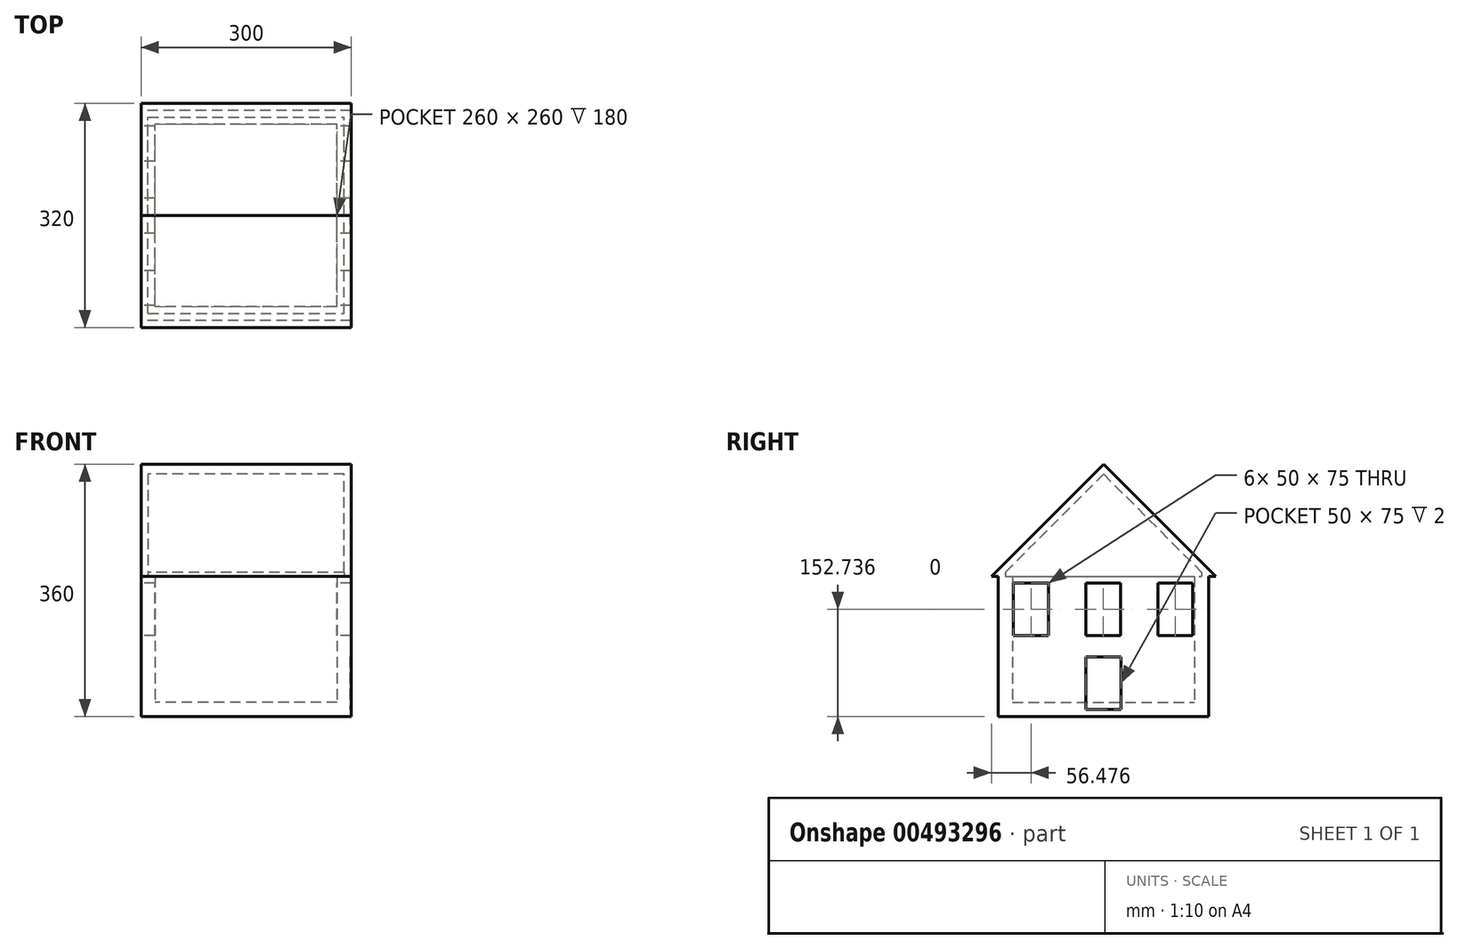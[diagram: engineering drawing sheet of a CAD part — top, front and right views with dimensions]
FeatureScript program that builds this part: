
annotation { "Feature Type Name" : "Feature", "Feature Type Description" : "" }
export const myFeature = defineFeature(function(context is Context, id is Id, definition is map)
    precondition{}
    {
        {
            var Q0;
            Q0=qCreatedBy(makeId("Top.planeOp"),FACE);
            var sketch = newSketch(context, id + "F0", { "sketchPlane" : qUnion([Q0])});
            skLineSegment(sketch, "E0.bottom", {"start": v(150, -150) * mm, "end": v(-150, -150) * mm});
            skLineSegment(sketch, "E0.top", {"start": v(150, 150) * mm, "end": v(-150, 150) * mm});
            skLineSegment(sketch, "E0.left", {"start": v(150, -150) * mm, "end": v(150, 150) * mm});
            skLineSegment(sketch, "E0.right", {"start": v(-150, -150) * mm, "end": v(-150, 150) * mm});
            skPoint(sketch, "E0.middle", {"position": v(0, 0) * mm});
            skSolve(sketch);
        }
        {
            var Q0;
            Q0=makeQuery(id+"F0.imprint","IMPRINT",FACE,{"disambiguationData":[TD([[makeQuery(id+"F0.imprint","IMPRINT",EDGE,{"derivedFrom":sQuery(id+"F0.wireOp",EDGE,"E0.bottom")}),-1.0]])]});
            extrude(context, id + "F1", {"entities" : qUnion([Q0]), "depth" : 200 * mm});
        }
        {
            var Q0;
            Q0=makeQuery(id+"F1.opExtrude","CAP_FACE",FACE,{"disambiguationData":[OSD([sQuery(id+"F0.wireOp",EDGE,"E0.bottom"),sQuery(id+"F0.wireOp",EDGE,"E0.top"),sQuery(id+"F0.wireOp",EDGE,"E0.left"),sQuery(id+"F0.wireOp",EDGE,"E0.right")])],"isStart":false});
            shell(context, id + "F2", {"entities" : qUnion([Q0]), "thickness" : 20 * mm});
        }
        {
            var Q0;
            Q0=qCreatedBy(makeId("Right.planeOp"),FACE);
            var sketch = newSketch(context, id + "F3", { "sketchPlane" : qUnion([Q0])});
            skLineSegment(sketch, "E1", {"start": v(0, 360) * mm, "end": v(160, 200) * mm});
            skLineSegment(sketch, "E2", {"start": v(160, 200) * mm, "end": v(-160, 200) * mm});
            skLineSegment(sketch, "E3", {"start": v(-160, 200) * mm, "end": v(0, 360) * mm});
            skSolve(sketch);
        }
        {
            var Q0;
            Q0 = qSketchRegion(id + "F3", true);
            extrude(context, id + "F4", {"entities" : qUnion([Q0]), "operationType" : NewBodyOperationType.ADD, "depth" : 300 * mm, "symmetric" : true});
        }
        {
            var Q0;
            Q0=makeQuery(id+"F4.boolean.opBoolean","MERGE",FACE,{"derivedFrom":[makeQuery(id+"F1.opExtrude","SWEPT_FACE",FACE,{"disambiguationData":[OSD([sQuery(id+"F0.wireOp",EDGE,"E0.right")])]}),makeQuery(id+"F4.opExtrude","CAP_FACE",FACE,{"disambiguationData":[OSD([sQuery(id+"F3.wireOp",EDGE,"E1"),sQuery(id+"F3.wireOp",EDGE,"E2"),sQuery(id+"F3.wireOp",EDGE,"E3")])],"isStart":true})]});
            var sketch = newSketch(context, id + "F5", { "sketchPlane" : qUnion([Q0])});
            skLineSegment(sketch, "E4.bottom", {"start": v(-77.48, 115.24) * mm, "end": v(-127.48, 115.24) * mm});
            skLineSegment(sketch, "E4.top", {"start": v(-77.48, 190.24) * mm, "end": v(-127.48, 190.24) * mm});
            skLineSegment(sketch, "E4.left", {"start": v(-77.48, 115.24) * mm, "end": v(-77.48, 190.24) * mm});
            skLineSegment(sketch, "E4.right", {"start": v(-127.48, 115.24) * mm, "end": v(-127.48, 190.24) * mm});
            skPoint(sketch, "E4.middle", {"position": v(-102.48, 152.74) * mm});
            skLineSegment(sketch, "E5.1.0.0", {"start": v(-24.48, 115.24) * mm, "end": v(-24.48, 190.24) * mm});
            skLineSegment(sketch, "E5.1.0.1", {"start": v(25.52, 115.24) * mm, "end": v(25.52, 190.24) * mm});
            skLineSegment(sketch, "E5.1.0.2", {"start": v(25.52, 190.24) * mm, "end": v(-24.48, 190.24) * mm});
            skLineSegment(sketch, "E5.1.0.3", {"start": v(25.52, 115.24) * mm, "end": v(-24.48, 115.24) * mm});
            skPoint(sketch, "E5.1.0.4", {"position": v(0.52, 152.74) * mm});
            skLineSegment(sketch, "E5.2.0.0", {"start": v(78.52, 115.24) * mm, "end": v(78.52, 190.24) * mm});
            skLineSegment(sketch, "E5.2.0.1", {"start": v(128.52, 115.24) * mm, "end": v(128.52, 190.24) * mm});
            skLineSegment(sketch, "E5.2.0.2", {"start": v(128.52, 190.24) * mm, "end": v(78.52, 190.24) * mm});
            skLineSegment(sketch, "E5.2.0.3", {"start": v(128.52, 115.24) * mm, "end": v(78.52, 115.24) * mm});
            skPoint(sketch, "E5.2.0.4", {"position": v(103.52, 152.74) * mm});
            skLineSegment(sketch, "E5.direction1", {"start": v(-127.48, 115.24) * mm, "end": v(-24.48, 115.24) * mm, "construction": true});
            skSolve(sketch);
        }
        {
            var Q0;
            Q0 = qSketchRegion(id + "F5", true);
            extrude(context, id + "F6", {"entities" : qUnion([Q0]), "operationType" : NewBodyOperationType.REMOVE, "endBound" : BoundingType.THROUGH_ALL, "oppositeDirection" : true, "depth" : 25 * mm});
        }
        {
            var Q0;
            Q0=makeQuery(id+"F4.boolean.opBoolean","SPLIT",FACE,{"disambiguationData":[TD([makeQuery(id+"F2.opShell","OFFSET_FACE",FACE,{"disambiguationData":[OSD([sQuery(id+"F0.wireOp",EDGE,"E0.bottom")])]})])],"derivedFrom":makeQuery(id+"F4.opExtrude","SWEPT_FACE",FACE,{"disambiguationData":[OSD([sQuery(id+"F3.wireOp",EDGE,"E2")])]})});
            shell(context, id + "F7", {"entities" : qUnion([Q0]), "thickness" : 10 * mm});
        }
        {
            var Q0;
            Q0=makeQuery(id+"F4.boolean.opBoolean","MERGE",FACE,{"derivedFrom":[makeQuery(id+"F1.opExtrude","SWEPT_FACE",FACE,{"disambiguationData":[OSD([sQuery(id+"F0.wireOp",EDGE,"E0.left")])]}),makeQuery(id+"F4.opExtrude","CAP_FACE",FACE,{"disambiguationData":[OSD([sQuery(id+"F3.wireOp",EDGE,"E1"),sQuery(id+"F3.wireOp",EDGE,"E2"),sQuery(id+"F3.wireOp",EDGE,"E3")])],"isStart":false})]});
            var sketch = newSketch(context, id + "F8", { "sketchPlane" : qUnion([Q0])});
            skLineSegment(sketch, "E6.bottom", {"start": v(25, 85) * mm, "end": v(-25, 85) * mm});
            skLineSegment(sketch, "E6.top", {"start": v(25, 10) * mm, "end": v(-25, 10) * mm});
            skLineSegment(sketch, "E6.left", {"start": v(25, 85) * mm, "end": v(25, 10) * mm});
            skLineSegment(sketch, "E6.right", {"start": v(-25, 85) * mm, "end": v(-25, 10) * mm});
            skPoint(sketch, "E6.middle", {"position": v(0, 47.5) * mm});
            skSolve(sketch);
        }
        {
            var Q0;
            Q0 = qSketchRegion(id + "F8", true);
            extrude(context, id + "F9", {"entities" : qUnion([Q0]), "operationType" : NewBodyOperationType.REMOVE, "oppositeDirection" : true, "depth" : 2 * mm});
        }
    });
